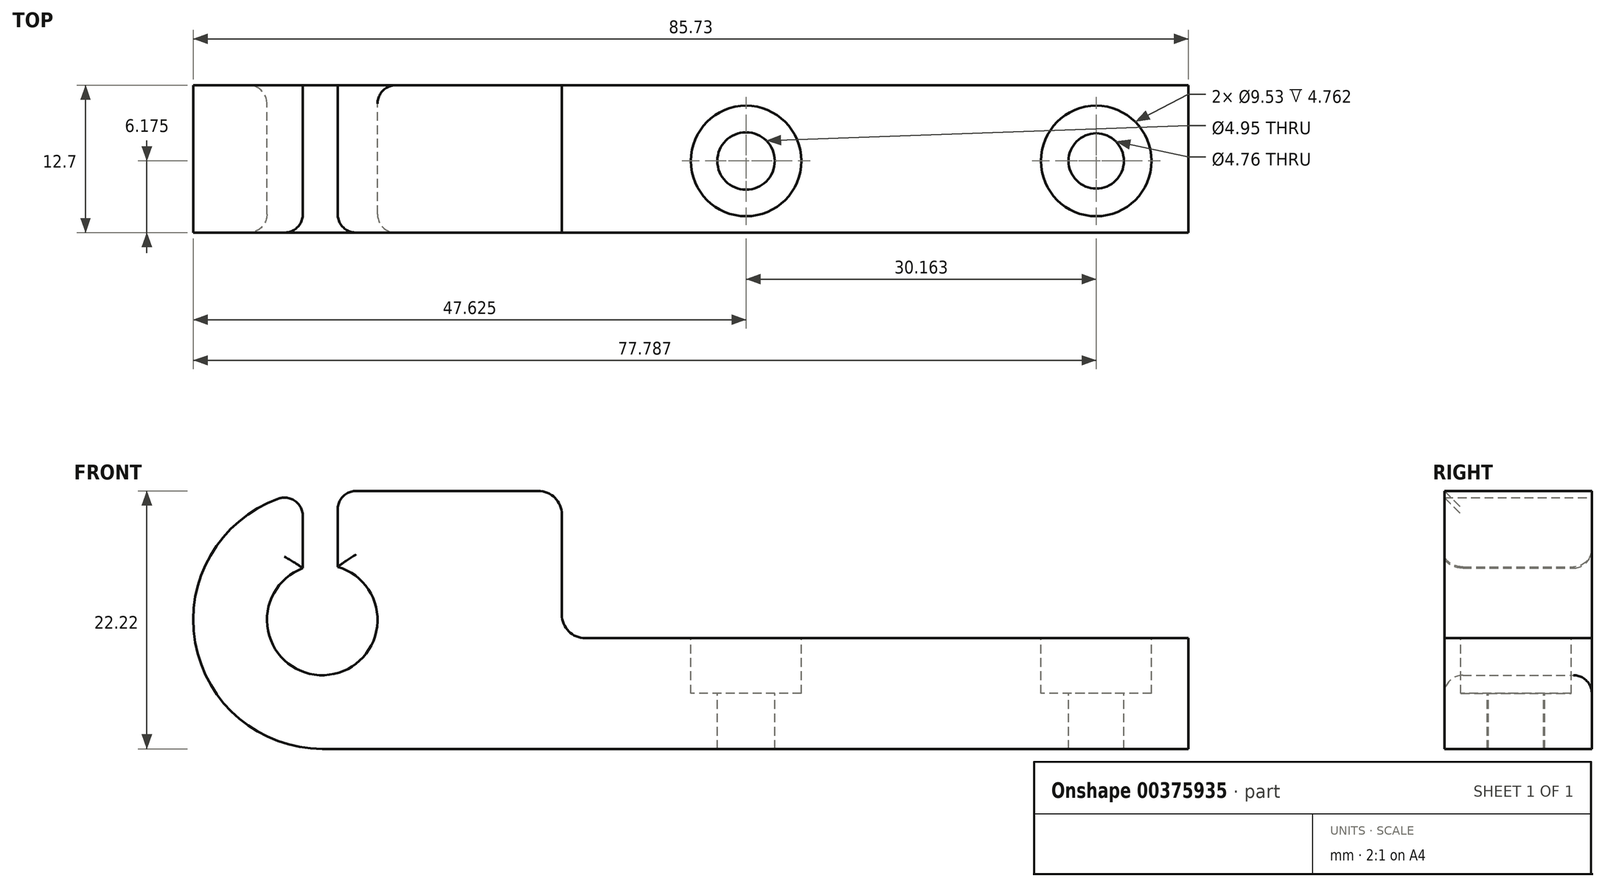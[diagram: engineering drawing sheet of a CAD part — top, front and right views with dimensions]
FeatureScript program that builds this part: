
annotation { "Feature Type Name" : "Feature", "Feature Type Description" : "" }
export const myFeature = defineFeature(function(context is Context, id is Id, definition is map)
    precondition{}
    {
        {
            var Q0;
            Q0=qCreatedBy(makeId("Front.planeOp"),FACE);
            var sketch = newSketch(context, id + "F0", { "sketchPlane" : qUnion([Q0])});
            skArc(sketch, "E0", {"start": v(-20.64, -8.32) * mm, "mid": v(-31.75, -19.43) * mm, "end": v(-20.64, -30.54) * mm});
            skCircle(sketch, "E1", {"center": v(-20.64, -19.43) * mm, "radius": 4.76 * mm});
            skLineSegment(sketch, "E2", {"start": v(-20.64, -8.32) * mm, "end": v(0, -8.32) * mm});
            skLineSegment(sketch, "E3", {"start": v(0, -21) * mm, "end": v(0, -8.32) * mm});
            skLineSegment(sketch, "E4", {"start": v(0, -21) * mm, "end": v(53.98, -21) * mm});
            skLineSegment(sketch, "E5", {"start": v(53.98, -21) * mm, "end": v(53.98, -30.54) * mm});
            skLineSegment(sketch, "E6", {"start": v(53.98, -30.54) * mm, "end": v(4.76, -30.54) * mm});
            skLineSegment(sketch, "E7", {"start": v(4.76, -30.54) * mm, "end": v(4.76, -30.54) * mm});
            skLineSegment(sketch, "E8", {"start": v(4.76, -30.54) * mm, "end": v(-20.64, -30.54) * mm});
            skSolve(sketch);
        }
        {
            var Q0;
            Q0 = qSketchRegion(id + "F0", true);
            extrude(context, id + "F1", {"entities" : qUnion([Q0]), "depth" : 12.7 * mm});
        }
        {
            var Q0;
            Q0=qCreatedBy(makeId("Front.planeOp"),FACE);
            var sketch = newSketch(context, id + "F2", { "sketchPlane" : qUnion([Q0])});
            skLineSegment(sketch, "E9", {"start": v(-22.3, -7.62) * mm, "end": v(-22.3, -16.61) * mm});
            skLineSegment(sketch, "E10", {"start": v(-22.3, -16.61) * mm, "end": v(-19.3, -16.61) * mm});
            skLineSegment(sketch, "E11", {"start": v(-19.3, -16.61) * mm, "end": v(-19.3, -7.78) * mm});
            skLineSegment(sketch, "E12", {"start": v(-19.3, -7.78) * mm, "end": v(-22.3, -7.62) * mm});
            skSolve(sketch);
        }
        {
            var Q0;
            Q0 = qSketchRegion(id + "F2", true);
            extrude(context, id + "F3", {"entities" : qUnion([Q0]), "operationType" : NewBodyOperationType.REMOVE, "endBound" : BoundingType.THROUGH_ALL, "depth" : 25.4 * mm});
        }
        {
            var Q0;
            Q0=makeQuery(id+"F3.boolean.opBoolean","INTERSECT",EDGE,{"derivedFrom":[makeQuery(id+"F1.opExtrude","SWEPT_FACE",FACE,{"disambiguationData":[OSD([sQuery(id+"F0.wireOp",EDGE,"E2")])]}),makeQuery(id+"F3.opExtrude","SWEPT_FACE",FACE,{"disambiguationData":[OSD([sQuery(id+"F2.wireOp",EDGE,"E11")])]})]});
            var Q1;
            Q1=makeQuery(id+"F3.boolean.opBoolean","INTERSECT",EDGE,{"derivedFrom":[makeQuery(id+"F1.opExtrude","SWEPT_FACE",FACE,{"disambiguationData":[OSD([sQuery(id+"F0.wireOp",EDGE,"E0")])]}),makeQuery(id+"F3.opExtrude","SWEPT_FACE",FACE,{"disambiguationData":[OSD([sQuery(id+"F2.wireOp",EDGE,"E9")])]})]});
            var Q2;
            Q2=makeQuery(id+"F3.boolean.opBoolean","INTERSECT",EDGE,{"derivedFrom":[makeQuery(id+"F1.opExtrude","CAP_FACE",FACE,{"disambiguationData":[OSD([sQuery(id+"F0.wireOp",EDGE,"E0"),sQuery(id+"F0.wireOp",EDGE,"E1"),sQuery(id+"F0.wireOp",EDGE,"E2"),sQuery(id+"F0.wireOp",EDGE,"E3"),sQuery(id+"F0.wireOp",EDGE,"E4"),sQuery(id+"F0.wireOp",EDGE,"E5"),sQuery(id+"F0.wireOp",EDGE,"E6"),sQuery(id+"F0.wireOp",EDGE,"E7"),sQuery(id+"F0.wireOp",EDGE,"E8")])],"isStart":false}),makeQuery(id+"F3.opExtrude","SWEPT_FACE",FACE,{"disambiguationData":[OSD([sQuery(id+"F2.wireOp",EDGE,"E9")])]})]});
            var Q3;
            Q3=makeQuery(id+"F3.boolean.opBoolean","INTERSECT",EDGE,{"derivedFrom":[makeQuery(id+"F1.opExtrude","CAP_FACE",FACE,{"disambiguationData":[OSD([sQuery(id+"F0.wireOp",EDGE,"E0"),sQuery(id+"F0.wireOp",EDGE,"E1"),sQuery(id+"F0.wireOp",EDGE,"E2"),sQuery(id+"F0.wireOp",EDGE,"E3"),sQuery(id+"F0.wireOp",EDGE,"E4"),sQuery(id+"F0.wireOp",EDGE,"E5"),sQuery(id+"F0.wireOp",EDGE,"E6"),sQuery(id+"F0.wireOp",EDGE,"E7"),sQuery(id+"F0.wireOp",EDGE,"E8")])],"isStart":false}),makeQuery(id+"F3.opExtrude","SWEPT_FACE",FACE,{"disambiguationData":[OSD([sQuery(id+"F2.wireOp",EDGE,"E11")])]})]});
            var Q4;
            Q4=makeQuery(id+"F1.opExtrude","CAP_EDGE",EDGE,{"disambiguationData":[OSD([sQuery(id+"F0.wireOp",EDGE,"E1")])],"isStart":false});
            var Q5;
            Q5=makeQuery(id+"F3.boolean.opBoolean","COPY",EDGE,{"derivedFrom":makeQuery(id+"F3.opExtrude","CAP_EDGE",EDGE,{"disambiguationData":[OSD([sQuery(id+"F2.wireOp",EDGE,"E11")])],"isStart":true})});
            var Q6;
            Q6=makeQuery(id+"F3.boolean.opBoolean","COPY",EDGE,{"derivedFrom":makeQuery(id+"F3.opExtrude","CAP_EDGE",EDGE,{"disambiguationData":[OSD([sQuery(id+"F2.wireOp",EDGE,"E9")])],"isStart":true})});
            var Q7;
            Q7=makeQuery(id+"F1.opExtrude","CAP_EDGE",EDGE,{"disambiguationData":[OSD([sQuery(id+"F0.wireOp",EDGE,"E1")])],"isStart":true});
            fillet(context, id + "F4", {"entities" : qUnion([Q0, Q1, Q2, Q3, Q4, Q5, Q6, Q7]), "radius" : 1.59 * mm, "tangentPropagation" : true, "allowEdgeOverflow" : false});
        }
        {
            var Q0;
            Q0=qCreatedBy(makeId("Top.planeOp"),FACE);
            var sketch = newSketch(context, id + "F5", { "sketchPlane" : qUnion([Q0])});
            skCircle(sketch, "E13", {"center": v(46.04, -6.52) * mm, "radius": 2.38 * mm});
            skCircle(sketch, "E14", {"center": v(15.88, -6.52) * mm, "radius": 2.48 * mm});
            skSolve(sketch);
        }
        {
            var Q0;
            Q0 = qSketchRegion(id + "F5", true);
            extrude(context, id + "F6", {"entities" : qUnion([Q0]), "operationType" : NewBodyOperationType.REMOVE, "depth" : 101.6 * mm});
        }
        {
            var Q0;
            Q0=makeQuery(id+"F1.opExtrude","SWEPT_FACE",FACE,{"disambiguationData":[OSD([sQuery(id+"F0.wireOp",EDGE,"E4")])]});
            var sketch = newSketch(context, id + "F7", { "sketchPlane" : qUnion([Q0])});
            skCircle(sketch, "E15", {"center": v(15.88, -6.52) * mm, "radius": 4.76 * mm});
            skCircle(sketch, "E16", {"center": v(46.04, -6.52) * mm, "radius": 4.76 * mm});
            skSolve(sketch);
        }
        {
            var Q0;
            Q0 = qSketchRegion(id + "F7", true);
            extrude(context, id + "F8", {"entities" : qUnion([Q0]), "operationType" : NewBodyOperationType.REMOVE, "oppositeDirection" : true, "depth" : 4.76 * mm});
        }
        {
            var Q0;
            Q0=makeQuery(id+"F5.imprint","IMPRINT",FACE,{"disambiguationData":[TD([[makeQuery(id+"F5.imprint","IMPRINT",EDGE,{"derivedFrom":sQuery(id+"F5.wireOp",EDGE,"E14")}),1.0]])]});
            var Q1;
            Q1=makeQuery(id+"F5.imprint","IMPRINT",FACE,{"disambiguationData":[TD([[makeQuery(id+"F5.imprint","IMPRINT",EDGE,{"derivedFrom":sQuery(id+"F5.wireOp",EDGE,"E13")}),1.0]])]});
            var Q2;
            Q2=sQuery(id+"F5.wireOp",EDGE,"E14");
            extrude(context, id + "F9", {"entities" : qUnion([Q0, Q1]), "operationType" : NewBodyOperationType.REMOVE, "surfaceEntities" : qUnion([Q2]), "oppositeDirection" : true, "depth" : 36.32 * mm});
        }
        {
            var Q0;
            Q0=makeQuery(id+"F1.opExtrude","SWEPT_EDGE",EDGE,{"disambiguationData":[OSD([sQuery(id+"F0.wireOp",EDGE,"E2"),sQuery(id+"F0.wireOp",EDGE,"E3")])]});
            var Q1;
            Q1=makeQuery(id+"F1.opExtrude","SWEPT_EDGE",EDGE,{"disambiguationData":[OSD([sQuery(id+"F0.wireOp",EDGE,"E3"),sQuery(id+"F0.wireOp",EDGE,"E4")])]});
            fillet(context, id + "F10", {"entities" : qUnion([Q0, Q1]), "radius" : 2.03 * mm, "tangentPropagation" : true, "allowEdgeOverflow" : false});
        }
    });
